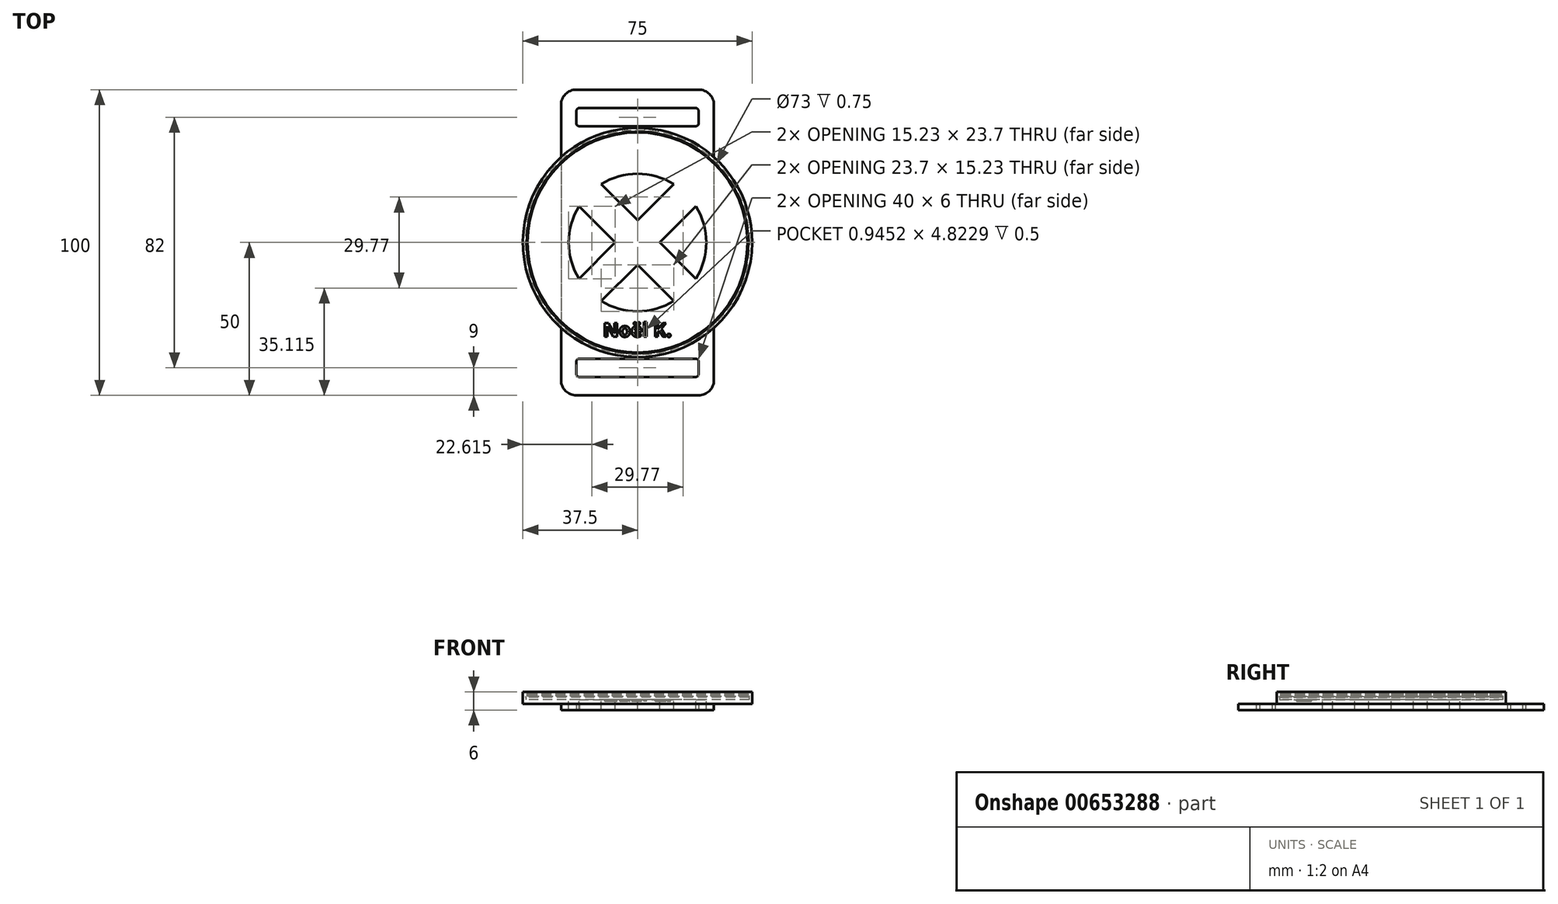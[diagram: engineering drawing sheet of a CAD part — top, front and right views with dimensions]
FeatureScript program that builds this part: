
annotation { "Feature Type Name" : "Feature", "Feature Type Description" : "" }
export const myFeature = defineFeature(function(context is Context, id is Id, definition is map)
    precondition{}
    {
        {
            var Q0;
            Q0=qCreatedBy(makeId("Top.planeOp"),FACE);
            var sketch = newSketch(context, id + "F0", { "sketchPlane" : qUnion([Q0])});
            skLineSegment(sketch, "E0.bottom", {"start": v(-25, 50) * mm, "end": v(25, 50) * mm});
            skLineSegment(sketch, "E0.top", {"start": v(-25, -50) * mm, "end": v(25, -50) * mm});
            skLineSegment(sketch, "E0.left", {"start": v(-25, 50) * mm, "end": v(-25, -50) * mm});
            skLineSegment(sketch, "E0.right", {"start": v(25, 50) * mm, "end": v(25, -50) * mm});
            skLineSegment(sketch, "E1", {"start": v(-25, 0) * mm, "end": v(25, 0) * mm, "construction": true});
            skLineSegment(sketch, "E2", {"start": v(0, -50) * mm, "end": v(0, 50) * mm, "construction": true});
            skPoint(sketch, "E3", {"position": v(0, 0) * mm});
            skSolve(sketch);
        }
        {
            var Q0;
            Q0=qSketchRegion(id+"F0",true);
            extrude(context, id + "F1", {"entities" : qUnion([Q0]), "depth" : 2 * mm, "offsetDistance" : 25 * mm});
        }
        {
            var Q0;
            Q0=makeQuery(id+"F1.opExtrude","CAP_FACE",FACE,{"disambiguationData":[OSD([sQuery(id+"F0.wireOp",EDGE,"E0.bottom"),sQuery(id+"F0.wireOp",EDGE,"E0.top"),sQuery(id+"F0.wireOp",EDGE,"E0.left"),sQuery(id+"F0.wireOp",EDGE,"E0.right")])],"isStart":false});
            var sketch = newSketch(context, id + "F2", { "sketchPlane" : qUnion([Q0])});
            skCircle(sketch, "E4", {"center": v(0, 0) * mm, "radius": 37.5 * mm});
            skSolve(sketch);
        }
        {
            var Q0;
            Q0=qSketchRegion(id+"F2",true);
            extrude(context, id + "F3", {"entities" : qUnion([Q0]), "operationType" : NewBodyOperationType.ADD, "depth" : 1.5 * mm, "offsetDistance" : 25 * mm});
        }
        {
            var Q0;
            Q0=makeQuery(id+"F3.opExtrude","CAP_FACE",FACE,{"disambiguationData":[OSD([sQuery(id+"F2.wireOp",EDGE,"E4")])],"isStart":false});
            var sketch = newSketch(context, id + "F4", { "sketchPlane" : qUnion([Q0])});
            skCircle(sketch, "E5", {"center": v(0, 0) * mm, "radius": 36.5 * mm});
            skSolve(sketch);
        }
        {
            var Q0;
            Q0=makeQuery(id+"F4.imprint","IMPRINT",FACE,{"disambiguationData":[TD([[makeQuery(id+"F4.imprint","IMPRINT",EDGE,{"derivedFrom":sQuery(id+"F4.wireOp",EDGE,"E5")}),-1.0]])]});
            extrude(context, id + "F5", {"entities" : qUnion([Q0]), "operationType" : NewBodyOperationType.ADD, "depth" : 1 * mm, "offsetDistance" : 25 * mm});
        }
        {
            var Q0;
            Q0=makeQuery(id+"F1.opExtrude","CAP_FACE",FACE,{"disambiguationData":[OSD([sQuery(id+"F0.wireOp",EDGE,"E0.bottom"),sQuery(id+"F0.wireOp",EDGE,"E0.top"),sQuery(id+"F0.wireOp",EDGE,"E0.left"),sQuery(id+"F0.wireOp",EDGE,"E0.right")])],"isStart":true});
            var sketch = newSketch(context, id + "F6", { "sketchPlane" : qUnion([Q0])});
            skLineSegment(sketch, "E6.bottom", {"start": v(-25, 40) * mm, "end": v(-22, 40) * mm});
            skLineSegment(sketch, "E6.top", {"start": v(-25, -40) * mm, "end": v(-22, -40) * mm});
            skLineSegment(sketch, "E6.left", {"start": v(-25, 40) * mm, "end": v(-25, -40) * mm});
            skLineSegment(sketch, "E6.right", {"start": v(-22, 40) * mm, "end": v(-22, -40) * mm});
            skLineSegment(sketch, "E7.bottom", {"start": v(22, 40) * mm, "end": v(25, 40) * mm});
            skLineSegment(sketch, "E7.top", {"start": v(22, -40) * mm, "end": v(25, -40) * mm});
            skLineSegment(sketch, "E7.left", {"start": v(22, 40) * mm, "end": v(22, -40) * mm});
            skLineSegment(sketch, "E7.right", {"start": v(25, 40) * mm, "end": v(25, -40) * mm});
            skSolve(sketch);
        }
        {
            var Q0;
            Q0=makeQuery(id+"F6.imprint","IMPRINT",FACE,{"disambiguationData":[TD([[makeQuery(id+"F6.imprint","IMPRINT",EDGE,{"derivedFrom":sQuery(id+"F6.wireOp",EDGE,"E6.bottom")}),-1.0]])]});
            var Q1;
            Q1=makeQuery(id+"F6.imprint","IMPRINT",FACE,{"disambiguationData":[TD([[makeQuery(id+"F6.imprint","IMPRINT",EDGE,{"derivedFrom":sQuery(id+"F6.wireOp",EDGE,"E7.bottom")}),-1.0]])]});
            extrude(context, id + "F7", {"entities" : qUnion([Q0, Q1]), "operationType" : NewBodyOperationType.ADD, "depth" : 3 * mm, "offsetDistance" : 25 * mm});
        }
        {
            var Q0;
            {var subQ0=sQuery(id+"F6.wireOp",EDGE,"E6.right");var subQ2=sQuery(id+"F6.wireOp",EDGE,"E6.left");var subQ3=sQuery(id+"F6.wireOp",EDGE,"E6.top");Q0=makeQuery(id+"Fcp3DyhTEGZhcjd_1.boolean.opBoolean","SPLIT",FACE,{"disambiguationData":[TD([makeQuery(id+"F7.opExtrude","SWEPT_FACE",FACE,{"disambiguationData":[OSD([subQ3])]})])],"derivedFrom":makeQuery(id+"F7.opExtrude","CAP_FACE",FACE,{"disambiguationData":[OSD([sQuery(id+"F6.wireOp",EDGE,"E6.bottom"),subQ3,subQ2,subQ0])],"isStart":false})});}
            var Q1;
            {var subQ0=sQuery(id+"F6.wireOp",EDGE,"E7.right");var subQ1=sQuery(id+"F6.wireOp",EDGE,"E7.left");var subQ2=sQuery(id+"F6.wireOp",EDGE,"E7.top");Q1=makeQuery(id+"Fcp3DyhTEGZhcjd_1.boolean.opBoolean","SPLIT",FACE,{"disambiguationData":[TD([makeQuery(id+"F7.opExtrude","SWEPT_FACE",FACE,{"disambiguationData":[OSD([subQ2])]})])],"derivedFrom":makeQuery(id+"F7.opExtrude","CAP_FACE",FACE,{"disambiguationData":[OSD([sQuery(id+"F6.wireOp",EDGE,"E7.bottom"),subQ2,subQ1,subQ0])],"isStart":false})});}
            var Q2;
            {var subQ0=sQuery(id+"F6.wireOp",EDGE,"E6.left");var subQ1=sQuery(id+"F6.wireOp",EDGE,"E6.right");var subQ3=sQuery(id+"F6.wireOp",EDGE,"E6.bottom");Q2=makeQuery(id+"Fcp3DyhTEGZhcjd_1.boolean.opBoolean","SPLIT",FACE,{"disambiguationData":[TD([makeQuery(id+"F7.opExtrude","SWEPT_FACE",FACE,{"disambiguationData":[OSD([subQ3])]})])],"derivedFrom":makeQuery(id+"F7.opExtrude","CAP_FACE",FACE,{"disambiguationData":[OSD([subQ3,sQuery(id+"F6.wireOp",EDGE,"E6.top"),subQ0,subQ1])],"isStart":false})});}
            var Q3;
            {var subQ0=sQuery(id+"F6.wireOp",EDGE,"E7.left");var subQ1=sQuery(id+"F6.wireOp",EDGE,"E7.right");var subQ2=sQuery(id+"F6.wireOp",EDGE,"E7.bottom");Q3=makeQuery(id+"Fcp3DyhTEGZhcjd_1.boolean.opBoolean","SPLIT",FACE,{"disambiguationData":[TD([makeQuery(id+"F7.opExtrude","SWEPT_FACE",FACE,{"disambiguationData":[OSD([subQ2])]})])],"derivedFrom":makeQuery(id+"F7.opExtrude","CAP_FACE",FACE,{"disambiguationData":[OSD([subQ2,sQuery(id+"F6.wireOp",EDGE,"E7.top"),subQ0,subQ1])],"isStart":false})});}
            var Q4;
            Q4=makeQuery(id+"F1.opExtrude","CAP_FACE",FACE,{"disambiguationData":[OSD([sQuery(id+"F0.wireOp",EDGE,"E0.bottom"),sQuery(id+"F0.wireOp",EDGE,"E0.top"),sQuery(id+"F0.wireOp",EDGE,"E0.left"),sQuery(id+"F0.wireOp",EDGE,"E0.right")])],"isStart":true});
            extrude(context, id + "F8", {"entities" : qUnion([Q0, Q1, Q2, Q3]), "operationType" : NewBodyOperationType.REMOVE, "endBound" : BoundingType.UP_TO_SURFACE, "oppositeDirection" : true, "depth" : 25 * mm, "endBoundEntityFace" : qUnion([Q4]), "offsetDistance" : 25 * mm});
        }
        {
            var Q0;
            Q0=makeQuery(id+"F3.opExtrude","CAP_FACE",FACE,{"disambiguationData":[OSD([sQuery(id+"F2.wireOp",EDGE,"E4")])],"isStart":false});
            var sketch = newSketch(context, id + "F9", { "sketchPlane" : qUnion([Q0])});
            skCircle(sketch, "E8", {"center": v(0, 0) * mm, "radius": 22.5 * mm});
            skLineSegment(sketch, "E9", {"start": v(19.13, -11.85) * mm, "end": v(7.27, 0) * mm});
            skLineSegment(sketch, "E10", {"start": v(-19.13, 11.85) * mm, "end": v(-7.27, 0) * mm});
            skLineSegment(sketch, "E11", {"start": v(19.13, 11.85) * mm, "end": v(7.27, 0) * mm});
            skLineSegment(sketch, "E12", {"start": v(-19.13, -11.85) * mm, "end": v(-7.27, 0) * mm});
            skLineSegment(sketch, "E13.trimOffspring", {"start": v(0, -7.27) * mm, "end": v(11.85, -19.13) * mm});
            skLineSegment(sketch, "E14.trimOffspring", {"start": v(0, 7.27) * mm, "end": v(11.85, 19.13) * mm});
            skLineSegment(sketch, "E15.trimOffspring", {"start": v(0, 7.27) * mm, "end": v(-11.85, 19.13) * mm});
            skLineSegment(sketch, "E16.trimOffspring", {"start": v(0, -7.27) * mm, "end": v(-11.85, -19.13) * mm});
            skLineSegment(sketch, "E17", {"start": v(0, 7.27) * mm, "end": v(0, 0) * mm, "construction": true});
            skLineSegment(sketch, "E18", {"start": v(-7.27, 0) * mm, "end": v(0, 0) * mm, "construction": true});
            skLineSegment(sketch, "E19", {"start": v(7.27, 0) * mm, "end": v(0, 0) * mm, "construction": true});
            skLineSegment(sketch, "E20", {"start": v(0, 0) * mm, "end": v(0, -7.27) * mm, "construction": true});
            skSolve(sketch);
        }
        {
            var Q0;
            {var subQ0=sQuery(id+"F9.wireOp",EDGE,"E10");Q0=makeQuery(id+"F9.imprint","IMPRINT",FACE,{"disambiguationData":[TD([[makeQuery(id+"F9.imprint","IMPRINT",EDGE,{"derivedFrom":subQ0}),-1.0]])]});}
            var Q1;
            {var subQ0=sQuery(id+"F9.wireOp",EDGE,"E13.trimOffspring");Q1=makeQuery(id+"F9.imprint","IMPRINT",FACE,{"disambiguationData":[TD([[makeQuery(id+"F9.imprint","IMPRINT",EDGE,{"derivedFrom":subQ0}),-1.0]])]});}
            var Q2;
            {var subQ0=sQuery(id+"F9.wireOp",EDGE,"E9");Q2=makeQuery(id+"F9.imprint","IMPRINT",FACE,{"disambiguationData":[TD([[makeQuery(id+"F9.imprint","IMPRINT",EDGE,{"derivedFrom":subQ0}),-1.0]])]});}
            var Q3;
            {var subQ0=sQuery(id+"F9.wireOp",EDGE,"E14.trimOffspring");Q3=makeQuery(id+"F9.imprint","IMPRINT",FACE,{"disambiguationData":[TD([[makeQuery(id+"F9.imprint","IMPRINT",EDGE,{"derivedFrom":subQ0}),1.0]])]});}
            extrude(context, id + "F10", {"entities" : qUnion([Q0, Q1, Q2, Q3]), "operationType" : NewBodyOperationType.REMOVE, "oppositeDirection" : true, "depth" : 25 * mm, "offsetDistance" : 25 * mm});
        }
        {
            var Q0;
            {var subQ0=sQuery(id+"F0.wireOp",EDGE,"E0.right");var subQ1=sQuery(id+"F0.wireOp",EDGE,"E0.left");var subQ2=sQuery(id+"F0.wireOp",EDGE,"E0.top");var subQ3=sQuery(id+"F0.wireOp",EDGE,"E0.bottom");Q0=makeQuery(id+"F8.boolean.opBoolean","MERGE",FACE,{"derivedFrom":[makeQuery(id+"F1.opExtrude","CAP_FACE",FACE,{"disambiguationData":[OSD([subQ3,subQ2,subQ1,subQ0])],"isStart":true}),makeQuery(id+"F8.opExtrude","CAP_FACE",FACE,{"disambiguationData":[OSD([subQ3,subQ2,subQ1,subQ0]),OD(0.0)],"isStart":false}),makeQuery(id+"F8.opExtrude","CAP_FACE",FACE,{"disambiguationData":[OSD([subQ3,subQ2,subQ1,subQ0]),OD(1.0)],"isStart":false}),makeQuery(id+"F8.opExtrude","CAP_FACE",FACE,{"disambiguationData":[OSD([subQ3,subQ2,subQ1,subQ0]),OD(2.0)],"isStart":false}),makeQuery(id+"F8.opExtrude","CAP_FACE",FACE,{"disambiguationData":[OSD([subQ3,subQ2,subQ1,subQ0]),OD(3.0)],"isStart":false})]});}
            var sketch = newSketch(context, id + "F11", { "sketchPlane" : qUnion([Q0])});
            skLineSegment(sketch, "E21.bottom", {"start": v(19, 44) * mm, "end": v(-19, 44) * mm});
            skLineSegment(sketch, "E21.top", {"start": v(19, 38) * mm, "end": v(-19, 38) * mm});
            skLineSegment(sketch, "E21.left", {"start": v(20, 43) * mm, "end": v(20, 39) * mm});
            skLineSegment(sketch, "E21.right", {"start": v(-20, 43) * mm, "end": v(-20, 39) * mm});
            skLineSegment(sketch, "E22.bottom", {"start": v(19, -38) * mm, "end": v(-19, -38) * mm});
            skLineSegment(sketch, "E22.top", {"start": v(19, -44) * mm, "end": v(-19, -44) * mm});
            skLineSegment(sketch, "E22.left", {"start": v(20, -39) * mm, "end": v(20, -43) * mm});
            skLineSegment(sketch, "E22.right", {"start": v(-20, -39) * mm, "end": v(-20, -43) * mm});
            skPoint(sketch, "E23.visualSharp", {"position": v(20, 44) * mm});
            skArc(sketch, "E23.filletArc", {"start": v(20, 43) * mm, "mid": v(19.7, 43.7) * mm, "end": v(19, 44) * mm});
            skPoint(sketch, "E24.visualSharp", {"position": v(20, 38) * mm});
            skArc(sketch, "E24.filletArc", {"start": v(19, 38) * mm, "mid": v(19.7, 38.3) * mm, "end": v(20, 39) * mm});
            skPoint(sketch, "E25.visualSharp", {"position": v(-20, 38) * mm});
            skArc(sketch, "E25.filletArc", {"start": v(-20, 39) * mm, "mid": v(-19.7, 38.3) * mm, "end": v(-19, 38) * mm});
            skPoint(sketch, "E26.visualSharp", {"position": v(-20, 44) * mm});
            skArc(sketch, "E26.filletArc", {"start": v(-19, 44) * mm, "mid": v(-19.7, 43.7) * mm, "end": v(-20, 43) * mm});
            skPoint(sketch, "E27.visualSharp", {"position": v(-20, -38) * mm});
            skArc(sketch, "E27.filletArc", {"start": v(-19, -38) * mm, "mid": v(-19.7, -38.3) * mm, "end": v(-20, -39) * mm});
            skPoint(sketch, "E28.visualSharp", {"position": v(-20, -44) * mm});
            skArc(sketch, "E28.filletArc", {"start": v(-20, -43) * mm, "mid": v(-19.7, -43.7) * mm, "end": v(-19, -44) * mm});
            skPoint(sketch, "E29.visualSharp", {"position": v(20, -44) * mm});
            skArc(sketch, "E29.filletArc", {"start": v(19, -44) * mm, "mid": v(19.7, -43.7) * mm, "end": v(20, -43) * mm});
            skPoint(sketch, "E30.visualSharp", {"position": v(20, -38) * mm});
            skArc(sketch, "E30.filletArc", {"start": v(20, -39) * mm, "mid": v(19.7, -38.3) * mm, "end": v(19, -38) * mm});
            skLineSegment(sketch, "E31.bottom", {"start": v(-4, 44) * mm, "end": v(4, 44) * mm});
            skLineSegment(sketch, "E31.top", {"start": v(-4, 50) * mm, "end": v(4, 50) * mm});
            skLineSegment(sketch, "E31.left", {"start": v(-4, 44) * mm, "end": v(-4, 50) * mm});
            skLineSegment(sketch, "E31.right", {"start": v(4, 44) * mm, "end": v(4, 50) * mm});
            skLineSegment(sketch, "E32.bottom", {"start": v(4, -44) * mm, "end": v(-4, -44) * mm});
            skLineSegment(sketch, "E32.top", {"start": v(4, -50) * mm, "end": v(-4, -50) * mm});
            skLineSegment(sketch, "E32.left", {"start": v(4, -44) * mm, "end": v(4, -50) * mm});
            skLineSegment(sketch, "E32.right", {"start": v(-4, -44) * mm, "end": v(-4, -50) * mm});
            skSolve(sketch);
        }
        {
            var Q0;
            Q0=makeQuery(id+"F11.imprint","IMPRINT",FACE,{"disambiguationData":[TD([[makeQuery(id+"F11.imprint","IMPRINT",EDGE,{"derivedFrom":sQuery(id+"F11.wireOp",EDGE,"E32.bottom")}),1.0]])]});
            var Q1;
            Q1=makeQuery(id+"F11.imprint","IMPRINT",FACE,{"disambiguationData":[TD([[makeQuery(id+"F11.imprint","IMPRINT",EDGE,{"derivedFrom":sQuery(id+"F11.wireOp",EDGE,"E22.bottom")}),1.0]])]});
            var Q2;
            Q2=makeQuery(id+"F11.imprint","IMPRINT",FACE,{"disambiguationData":[TD([[makeQuery(id+"F11.imprint","IMPRINT",EDGE,{"derivedFrom":sQuery(id+"F11.wireOp",EDGE,"E31.bottom")}),1.0]])]});
            var Q3;
            Q3=makeQuery(id+"F11.imprint","IMPRINT",FACE,{"disambiguationData":[TD([[makeQuery(id+"F11.imprint","IMPRINT",EDGE,{"derivedFrom":sQuery(id+"F11.wireOp",EDGE,"E21.top")}),-1.0]])]});
            extrude(context, id + "F12", {"entities" : qUnion([Q0, Q1, Q2, Q3]), "operationType" : NewBodyOperationType.REMOVE, "oppositeDirection" : true, "depth" : 25 * mm, "offsetDistance" : 25 * mm});
        }
        {
            var Q0;
            Q0=makeQuery(id+"F12.boolean.opBoolean","COPY",EDGE,{"derivedFrom":makeQuery(id+"F12.opExtrude","SWEPT_EDGE",EDGE,{"disambiguationData":[OSD([sQuery(id+"F0.wireOp",EDGE,"E0.top"),sQuery(id+"F11.wireOp",EDGE,"E31.top"),sQuery(id+"F11.wireOp",EDGE,"E31.left")])]})});
            var Q1;
            Q1=makeQuery(id+"F12.boolean.opBoolean","COPY",EDGE,{"derivedFrom":makeQuery(id+"F12.opExtrude","SWEPT_EDGE",EDGE,{"disambiguationData":[OSD([sQuery(id+"F11.wireOp",EDGE,"E21.bottom"),sQuery(id+"F11.wireOp",EDGE,"E31.bottom"),sQuery(id+"F11.wireOp",EDGE,"E31.left")])]})});
            var Q2;
            Q2=makeQuery(id+"F12.boolean.opBoolean","COPY",EDGE,{"derivedFrom":makeQuery(id+"F12.opExtrude","SWEPT_EDGE",EDGE,{"disambiguationData":[OSD([sQuery(id+"F0.wireOp",EDGE,"E0.top"),sQuery(id+"F11.wireOp",EDGE,"E31.top"),sQuery(id+"F11.wireOp",EDGE,"E31.right")])]})});
            var Q3;
            Q3=makeQuery(id+"F12.boolean.opBoolean","COPY",EDGE,{"derivedFrom":makeQuery(id+"F12.opExtrude","SWEPT_EDGE",EDGE,{"disambiguationData":[OSD([sQuery(id+"F11.wireOp",EDGE,"E21.bottom"),sQuery(id+"F11.wireOp",EDGE,"E31.bottom"),sQuery(id+"F11.wireOp",EDGE,"E31.right")])]})});
            fillet(context, id + "F13", {"entities" : qUnion([Q0, Q1, Q2, Q3]), "radius" : 1 * mm, "tangentPropagation" : true, "allowEdgeOverflow" : false});
        }
        {
            var Q0;
            Q0=makeQuery(id+"F12.boolean.opBoolean","COPY",EDGE,{"derivedFrom":makeQuery(id+"F12.opExtrude","SWEPT_EDGE",EDGE,{"disambiguationData":[OSD([sQuery(id+"F0.wireOp",EDGE,"E0.bottom"),sQuery(id+"F11.wireOp",EDGE,"E32.top"),sQuery(id+"F11.wireOp",EDGE,"E32.left")])]})});
            var Q1;
            Q1=makeQuery(id+"F12.boolean.opBoolean","COPY",EDGE,{"derivedFrom":makeQuery(id+"F12.opExtrude","SWEPT_EDGE",EDGE,{"disambiguationData":[OSD([sQuery(id+"F11.wireOp",EDGE,"E22.top"),sQuery(id+"F11.wireOp",EDGE,"E32.bottom"),sQuery(id+"F11.wireOp",EDGE,"E32.left")])]})});
            var Q2;
            Q2=makeQuery(id+"F12.boolean.opBoolean","COPY",EDGE,{"derivedFrom":makeQuery(id+"F12.opExtrude","SWEPT_EDGE",EDGE,{"disambiguationData":[OSD([sQuery(id+"F0.wireOp",EDGE,"E0.bottom"),sQuery(id+"F11.wireOp",EDGE,"E32.top"),sQuery(id+"F11.wireOp",EDGE,"E32.right")])]})});
            var Q3;
            Q3=makeQuery(id+"F12.boolean.opBoolean","COPY",EDGE,{"derivedFrom":makeQuery(id+"F12.opExtrude","SWEPT_EDGE",EDGE,{"disambiguationData":[OSD([sQuery(id+"F11.wireOp",EDGE,"E22.top"),sQuery(id+"F11.wireOp",EDGE,"E32.bottom"),sQuery(id+"F11.wireOp",EDGE,"E32.right")])]})});
            fillet(context, id + "F14", {"entities" : qUnion([Q0, Q1, Q2, Q3]), "radius" : 1 * mm, "tangentPropagation" : true, "allowEdgeOverflow" : false});
        }
        {
            var Q0;
            Q0=makeQuery(id+"F1.opExtrude","SWEPT_EDGE",EDGE,{"disambiguationData":[OSD([sQuery(id+"F0.wireOp",EDGE,"E0.top"),sQuery(id+"F0.wireOp",EDGE,"E0.right")])]});
            var Q1;
            Q1=makeQuery(id+"F1.opExtrude","SWEPT_EDGE",EDGE,{"disambiguationData":[OSD([sQuery(id+"F0.wireOp",EDGE,"E0.bottom"),sQuery(id+"F0.wireOp",EDGE,"E0.right")])]});
            var Q2;
            Q2=makeQuery(id+"F1.opExtrude","SWEPT_EDGE",EDGE,{"disambiguationData":[OSD([sQuery(id+"F0.wireOp",EDGE,"E0.bottom"),sQuery(id+"F0.wireOp",EDGE,"E0.left")])]});
            var Q3;
            Q3=makeQuery(id+"F1.opExtrude","SWEPT_EDGE",EDGE,{"disambiguationData":[OSD([sQuery(id+"F0.wireOp",EDGE,"E0.top"),sQuery(id+"F0.wireOp",EDGE,"E0.left")])]});
            fillet(context, id + "F15", {"entities" : qUnion([Q0, Q1, Q2, Q3]), "radius" : 5 * mm, "tangentPropagation" : true, "allowEdgeOverflow" : false});
        }
        {
            var Q0;
            Q0=makeQuery(id+"F1.opExtrude","SWEPT_BODY",BODY,{"disambiguationData":[OSD([sQuery(id+"F0.wireOp",EDGE,"E0.bottom"),sQuery(id+"F0.wireOp",EDGE,"E0.top"),sQuery(id+"F0.wireOp",EDGE,"E0.left"),sQuery(id+"F0.wireOp",EDGE,"E0.right")])]});
            transform(context, id + "F16", {"entities" : qUnion([Q0]), "transformType" : TransformType.TRANSLATION_3D, "dx" : 72.1 * mm, "dy" : 0 * mm, "dz" : 0 * mm, "makeCopy" : true});
        }
        {
            var Q0;
            Q0=makeQuery(id+"F16.opPattern","COPY",BODY,{"derivedFrom":makeQuery(id+"F1.opExtrude","SWEPT_BODY",BODY,{"disambiguationData":[OSD([sQuery(id+"F0.wireOp",EDGE,"E0.bottom"),sQuery(id+"F0.wireOp",EDGE,"E0.top"),sQuery(id+"F0.wireOp",EDGE,"E0.left"),sQuery(id+"F0.wireOp",EDGE,"E0.right")])]}),"instanceName":"1"});
            deleteBodies(context, id + "F17", {"entities" : qUnion([Q0])});
        }
        {
            var Q0;
            Q0=makeQuery(id+"F5.opExtrude","CAP_EDGE",EDGE,{"disambiguationData":[OSD([sQuery(id+"F4.wireOp",EDGE,"E5")])],"isStart":false});
            chamfer(context, id + "F18", {"entities" : qUnion([Q0]), "width" : 0.25 * mm, "tangentPropagation" : true});
        }
        {
            var Q0;
            Q0=makeQuery(id+"F5.opExtrude","CAP_FACE",FACE,{"disambiguationData":[OSD([sQuery(id+"F2.wireOp",EDGE,"E4"),sQuery(id+"F4.wireOp",EDGE,"E5")])],"isStart":false});
            var sketch = newSketch(context, id + "F19", { "sketchPlane" : qUnion([Q0])});
            skCircle(sketch, "E33", {"center": v(0, 0) * mm, "radius": 36 * mm});
            skSolve(sketch);
        }
        {
            var Q0;
            Q0=makeQuery(id+"F19.imprint","IMPRINT",FACE,{"disambiguationData":[TD([[makeQuery(id+"F19.imprint","IMPRINT",EDGE,{"derivedFrom":sQuery(id+"F19.wireOp",EDGE,"E33")}),-1.0]])]});
            var Q1;
            {var subQ0=sQuery(id+"F2.wireOp",EDGE,"E4");Q1=makeQuery(id+"F19.imprint","IMPRINT",FACE,{"disambiguationData":[TD([[makeQuery(id+"F19.imprint","IMPRINT",EDGE,{"derivedFrom":makeQuery(id+"F5.opExtrude","CAP_EDGE",EDGE,{"disambiguationData":[OSD([subQ0])],"isStart":false})}),1.0]])]});}
            extrude(context, id + "F20", {"entities" : qUnion([Q0, Q1]), "operationType" : NewBodyOperationType.ADD, "depth" : 0.5 * mm, "offsetDistance" : 25 * mm});
        }
        {
            var Q0;
            Q0=makeQuery(id+"F20.opExtrude","CAP_EDGE",EDGE,{"disambiguationData":[OSD([sQuery(id+"F19.wireOp",EDGE,"E33")])],"isStart":true});
            var Q1;
            Q1=makeQuery(id+"F20.opExtrude","CAP_EDGE",EDGE,{"disambiguationData":[OSD([sQuery(id+"F19.wireOp",EDGE,"E33")])],"isStart":false});
            chamfer(context, id + "F21", {"entities" : qUnion([Q0, Q1]), "width" : 0.25 * mm, "tangentPropagation" : true});
        }
        {
            var Q0;
            Q0=makeQuery(id+"F20.opExtrude","CAP_FACE",FACE,{"disambiguationData":[OSD([sQuery(id+"F2.wireOp",EDGE,"E4"),sQuery(id+"F19.wireOp",EDGE,"E33")])],"isStart":false});
            var sketch = newSketch(context, id + "F22", { "sketchPlane" : qUnion([Q0])});
            skCircle(sketch, "E34", {"center": v(0, 0) * mm, "radius": 36 * mm});
            skSolve(sketch);
        }
        {
            var Q0;
            Q0=makeQuery(id+"F22.imprint","IMPRINT",FACE,{"disambiguationData":[TD([[makeQuery(id+"F22.imprint","IMPRINT",EDGE,{"derivedFrom":sQuery(id+"F22.wireOp",EDGE,"E34")}),-1.0]])]});
            var Q1;
            {var subQ0=sQuery(id+"F2.wireOp",EDGE,"E4");Q1=makeQuery(id+"F22.imprint","IMPRINT",FACE,{"disambiguationData":[TD([[makeQuery(id+"F22.imprint","IMPRINT",EDGE,{"derivedFrom":makeQuery(id+"F20.opExtrude","CAP_EDGE",EDGE,{"disambiguationData":[OSD([subQ0])],"isStart":false})}),1.0]])]});}
            extrude(context, id + "F23", {"entities" : qUnion([Q0, Q1]), "operationType" : NewBodyOperationType.ADD, "depth" : 0.5 * mm, "offsetDistance" : 25 * mm});
        }
        {
            var Q0;
            Q0=makeQuery(id+"F23.opExtrude","CAP_EDGE",EDGE,{"disambiguationData":[OSD([sQuery(id+"F22.wireOp",EDGE,"E34")])],"isStart":true});
            var Q1;
            Q1=makeQuery(id+"F23.opExtrude","CAP_EDGE",EDGE,{"disambiguationData":[OSD([sQuery(id+"F22.wireOp",EDGE,"E34")])],"isStart":false});
            chamfer(context, id + "F24", {"entities" : qUnion([Q0, Q1]), "width" : 0.25 * mm, "tangentPropagation" : true});
        }
        {
            var Q0;
            Q0=makeQuery(id+"F23.opExtrude","CAP_FACE",FACE,{"disambiguationData":[OSD([sQuery(id+"F2.wireOp",EDGE,"E4"),sQuery(id+"F22.wireOp",EDGE,"E34")])],"isStart":false});
            var sketch = newSketch(context, id + "F25", { "sketchPlane" : qUnion([Q0])});
            skCircle(sketch, "E35", {"center": v(0, 0) * mm, "radius": 36 * mm});
            skSolve(sketch);
        }
        {
            var Q0;
            Q0=makeQuery(id+"F25.imprint","IMPRINT",FACE,{"disambiguationData":[TD([[makeQuery(id+"F25.imprint","IMPRINT",EDGE,{"derivedFrom":sQuery(id+"F25.wireOp",EDGE,"E35")}),-1.0]])]});
            var Q1;
            {var subQ0=sQuery(id+"F2.wireOp",EDGE,"E4");Q1=makeQuery(id+"F25.imprint","IMPRINT",FACE,{"disambiguationData":[TD([[makeQuery(id+"F25.imprint","IMPRINT",EDGE,{"derivedFrom":makeQuery(id+"F23.opExtrude","CAP_EDGE",EDGE,{"disambiguationData":[OSD([subQ0])],"isStart":false})}),1.0]])]});}
            extrude(context, id + "F26", {"entities" : qUnion([Q0, Q1]), "operationType" : NewBodyOperationType.ADD, "depth" : 0.5 * mm, "offsetDistance" : 25 * mm});
        }
        {
            var Q0;
            Q0=makeQuery(id+"F26.opExtrude","CAP_EDGE",EDGE,{"disambiguationData":[OSD([sQuery(id+"F25.wireOp",EDGE,"E35")])],"isStart":false});
            var Q1;
            Q1=makeQuery(id+"F26.opExtrude","CAP_EDGE",EDGE,{"disambiguationData":[OSD([sQuery(id+"F25.wireOp",EDGE,"E35")])],"isStart":true});
            chamfer(context, id + "F27", {"entities" : qUnion([Q0, Q1]), "width" : 0.25 * mm, "tangentPropagation" : true});
        }
        {
            var Q0;
            Q0=makeQuery(id+"F3.opExtrude","CAP_FACE",FACE,{"disambiguationData":[OSD([sQuery(id+"F2.wireOp",EDGE,"E4")])],"isStart":false});
            var sketch = newSketch(context, id + "F28", { "sketchPlane" : qUnion([Q0])});
            skText(sketch, "E36", { "text": "Noël K.", "fontName": "OpenSans-Bold.ttf"});
            const initialGuessF28  = {"E36": [-0.01126, -0.03084, 1, 0, 0.00457]};
            skSetInitialGuess(sketch, initialGuessF28);
            skSolve(sketch);
        }
        {
            var Q0;
            Q0=makeQuery(id+"F28.imprint","IMPRINT",FACE,{"disambiguationData":[TD([[makeQuery(id+"F28.imprint","IMPRINT",EDGE,{"derivedFrom":sQuery(id+"F28.wireOp",EDGE,"E36.sketch_text.stroke-85")}),-1.0]])]});
            var Q1;
            Q1=makeQuery(id+"F28.imprint","IMPRINT",FACE,{"disambiguationData":[TD([[makeQuery(id+"F28.imprint","IMPRINT",EDGE,{"derivedFrom":sQuery(id+"F28.wireOp",EDGE,"E36.sketch_text.stroke-72")}),-1.0]])]});
            var Q2;
            Q2=makeQuery(id+"F28.imprint","IMPRINT",FACE,{"disambiguationData":[TD([[makeQuery(id+"F28.imprint","IMPRINT",EDGE,{"derivedFrom":sQuery(id+"F28.wireOp",EDGE,"E36.sketch_text.stroke-68")}),-1.0]])]});
            var Q3;
            Q3=makeQuery(id+"F28.imprint","IMPRINT",FACE,{"disambiguationData":[TD([[makeQuery(id+"F28.imprint","IMPRINT",EDGE,{"derivedFrom":sQuery(id+"F28.wireOp",EDGE,"E36.sketch_text.stroke-32")}),-1.0]])]});
            var Q4;
            Q4=makeQuery(id+"F28.imprint","IMPRINT",FACE,{"disambiguationData":[TD([[makeQuery(id+"F28.imprint","IMPRINT",EDGE,{"derivedFrom":sQuery(id+"F28.wireOp",EDGE,"E36.sketch_text.stroke-52")}),-1.0]])]});
            var Q5;
            Q5=makeQuery(id+"F28.imprint","IMPRINT",FACE,{"disambiguationData":[TD([[makeQuery(id+"F28.imprint","IMPRINT",EDGE,{"derivedFrom":sQuery(id+"F28.wireOp",EDGE,"E36.sketch_text.stroke-60")}),-1.0]])]});
            var Q6;
            Q6=makeQuery(id+"F28.imprint","IMPRINT",FACE,{"disambiguationData":[TD([[makeQuery(id+"F28.imprint","IMPRINT",EDGE,{"derivedFrom":sQuery(id+"F28.wireOp",EDGE,"E36.sketch_text.stroke-14")}),-1.0]])]});
            var Q7;
            Q7=makeQuery(id+"F28.imprint","IMPRINT",FACE,{"disambiguationData":[TD([[makeQuery(id+"F28.imprint","IMPRINT",EDGE,{"derivedFrom":sQuery(id+"F28.wireOp",EDGE,"E36.sketch_text.stroke-0")}),-1.0]])]});
            extrude(context, id + "F29", {"entities" : qUnion([Q0, Q1, Q2, Q3, Q4, Q5, Q6, Q7]), "operationType" : NewBodyOperationType.REMOVE, "oppositeDirection" : true, "depth" : 0.5 * mm, "offsetDistance" : 25 * mm});
        }
    });
